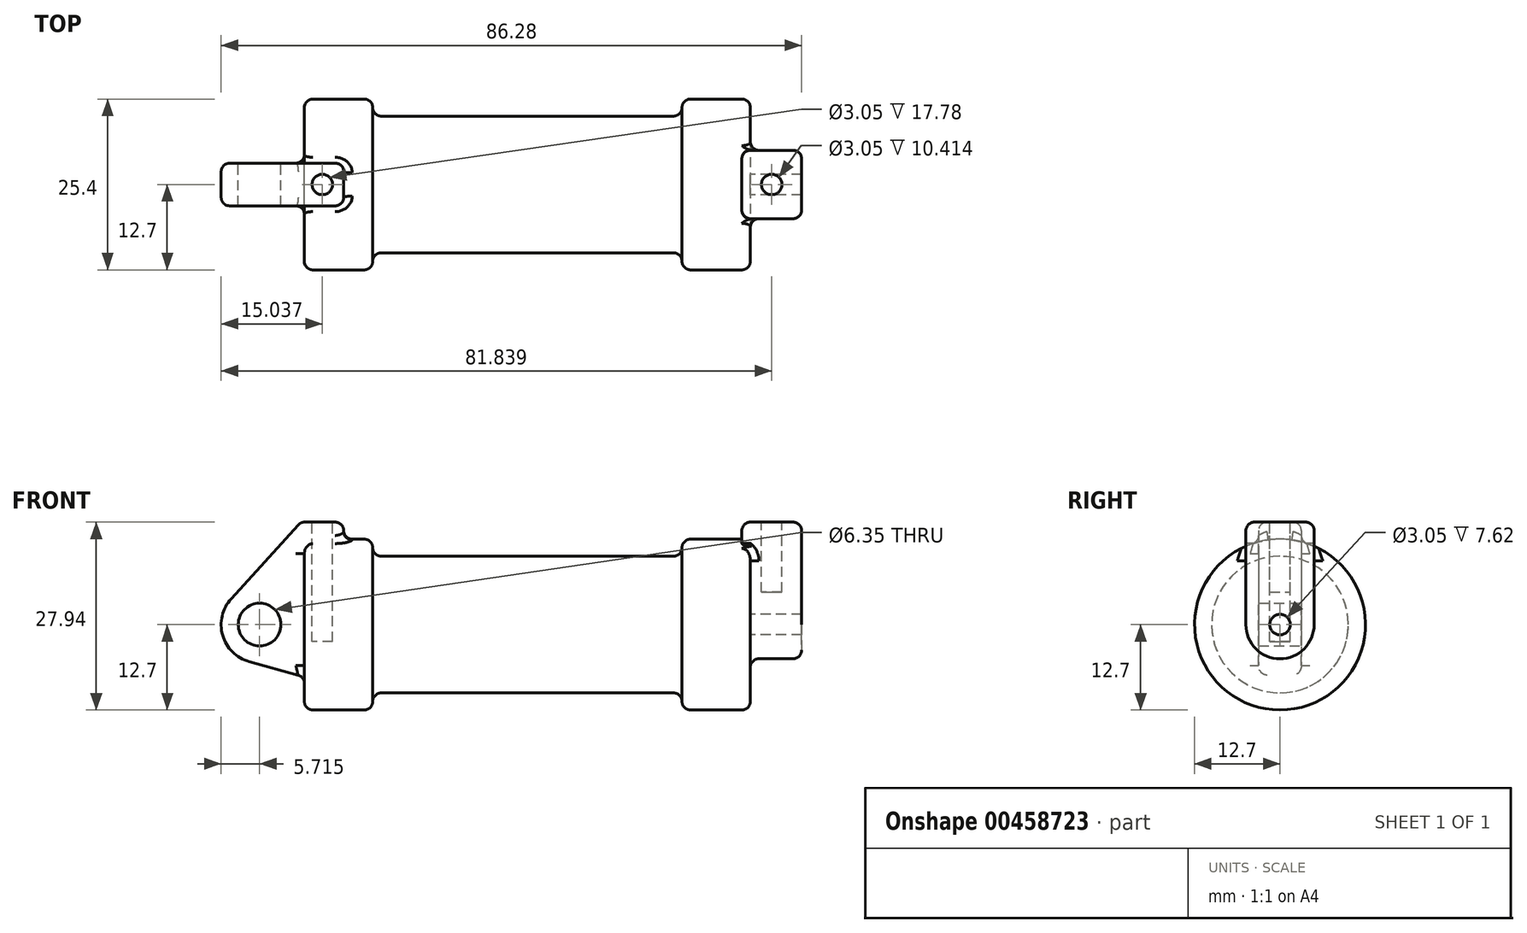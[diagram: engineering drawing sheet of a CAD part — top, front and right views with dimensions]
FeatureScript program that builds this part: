
annotation { "Feature Type Name" : "Feature", "Feature Type Description" : "" }
export const myFeature = defineFeature(function(context is Context, id is Id, definition is map)
    precondition{}
    {
        {
            var Q0;
            Q0=qCreatedBy(makeId("Front.planeOp"),FACE);
            var sketch = newSketch(context, id + "F0", { "sketchPlane" : qUnion([Q0])});
            skLineSegment(sketch, "E0", {"start": v(0, 0) * mm, "end": v(0, 12.7) * mm});
            skLineSegment(sketch, "E1", {"start": v(0, 12.7) * mm, "end": v(10.16, 12.7) * mm});
            skLineSegment(sketch, "E2", {"start": v(10.16, 12.7) * mm, "end": v(10.16, 10.16) * mm});
            skLineSegment(sketch, "E3", {"start": v(10.16, 10.16) * mm, "end": v(56.13, 10.16) * mm});
            skLineSegment(sketch, "E4", {"start": v(56.13, 10.16) * mm, "end": v(56.13, 12.7) * mm});
            skLineSegment(sketch, "E5", {"start": v(56.13, 12.7) * mm, "end": v(66.3, 12.7) * mm});
            skLineSegment(sketch, "E6", {"start": v(66.3, 12.7) * mm, "end": v(66.3, 0) * mm});
            skLineSegment(sketch, "E7", {"start": v(66.3, 0) * mm, "end": v(0, 0) * mm});
            skLineSegment(sketch, "E8", {"start": v(5.84, 15.24) * mm, "end": v(-0.5, 15.24) * mm});
            skLineSegment(sketch, "E9", {"start": v(-0.5, 15.24) * mm, "end": v(-10.88, 3.85) * mm});
            skLineSegment(sketch, "E10", {"start": v(0, 0) * mm, "end": v(-6.65, 0) * mm});
            skCircle(sketch, "E11", {"center": v(-6.65, 0) * mm, "radius": 5.72 * mm});
            skCircle(sketch, "E12", {"center": v(-6.65, 0) * mm, "radius": 3.18 * mm});
            skLineSegment(sketch, "E13", {"start": v(5.84, 15.24) * mm, "end": v(5.84, -9.4) * mm});
            skLineSegment(sketch, "E14", {"start": v(5.84, -9.4) * mm, "end": v(-8.18, -5.5) * mm});
            skSolve(sketch);
        }
        {
            var Q0;
            {var subQ0=sQuery(id+"F0.wireOp",EDGE,"E2");Q0=makeQuery(id+"F0.imprint","IMPRINT",FACE,{"disambiguationData":[TD([[makeQuery(id+"F0.imprint","IMPRINT",EDGE,{"derivedFrom":subQ0}),-1.0]])]});}
            var Q1;
            {var subQ0=sQuery(id+"F0.wireOp",EDGE,"E0");Q1=makeQuery(id+"F0.imprint","IMPRINT",FACE,{"disambiguationData":[TD([[makeQuery(id+"F0.imprint","IMPRINT",EDGE,{"derivedFrom":subQ0}),-1.0]])]});}
            var Q2;
            Q2=sQuery(id+"F0.wireOp",EDGE,"E7");
            revolve(context, id + "F1", {"entities" : qUnion([Q0, Q1]), "axis" : qUnion([Q2]), "revolveType" : RevolveType.FULL});
        }
        {
            var Q0;
            {var subQ1=sQuery(id+"F0.wireOp",EDGE,"E0");Q0=makeQuery(id+"F0.imprint","IMPRINT",FACE,{"disambiguationData":[TD([[makeQuery(id+"F0.imprint","IMPRINT",EDGE,{"derivedFrom":subQ1}),1.0]])]});}
            var Q1;
            {var subQ5=sQuery(id+"F0.wireOp",EDGE,"E12");Q1=makeQuery(id+"F0.imprint","IMPRINT",FACE,{"disambiguationData":[TD([[makeQuery(id+"F0.imprint","IMPRINT",EDGE,{"derivedFrom":subQ5}),-1.0]])]});}
            var Q2;
            {var subQ0=sQuery(id+"F0.wireOp",EDGE,"E14");Q2=makeQuery(id+"F0.imprint","IMPRINT",FACE,{"disambiguationData":[TD([[makeQuery(id+"F0.imprint","IMPRINT",EDGE,{"derivedFrom":subQ0}),-1.0]])]});}
            var Q3;
            {var subQ0=sQuery(id+"F0.wireOp",EDGE,"E0");Q3=makeQuery(id+"F0.imprint","IMPRINT",FACE,{"disambiguationData":[TD([[makeQuery(id+"F0.imprint","IMPRINT",EDGE,{"derivedFrom":subQ0}),-1.0]])]});}
            extrude(context, id + "F2", {"entities" : qUnion([Q0, Q1, Q2, Q3]), "operationType" : NewBodyOperationType.ADD, "depth" : 6.35 * mm, "symmetric" : true});
        }
        {
            var Q0;
            Q0=makeQuery(id+"F1.opRevolve","SWEPT_FACE",FACE,{"disambiguationData":[OSD([sQuery(id+"F0.wireOp",EDGE,"E6")])]});
            var sketch = newSketch(context, id + "F3", { "sketchPlane" : qUnion([Q0])});
            skLineSegment(sketch, "E15", {"start": v(-5.08, 15.23) * mm, "end": v(5.08, 15.23) * mm});
            skLineSegment(sketch, "E16", {"start": v(5.08, 15.23) * mm, "end": v(5.08, -0.01) * mm});
            skLineSegment(sketch, "E17", {"start": v(5.08, -0.01) * mm, "end": v(-5.08, -0.01) * mm});
            skLineSegment(sketch, "E18", {"start": v(-5.08, -0.01) * mm, "end": v(-5.08, 15.23) * mm});
            skCircle(sketch, "E19", {"center": v(0, 0) * mm, "radius": 5.08 * mm});
            skCircle(sketch, "E20", {"center": v(0, 0) * mm, "radius": 1.52 * mm});
            skLineSegment(sketch, "E21.MirrorCS", {"start": v(-5.08, 15.23) * mm, "end": v(-5.08, -0.01) * mm});
            skSolve(sketch);
        }
        {
            var Q0;
            {var subQ0=sQuery(id+"F3.wireOp",EDGE,"E19");var subQ1=sQuery(id+"F3.wireOp",EDGE,"E16");var subQ2=makeQuery(id+"F3.imprint","INTERSECT",VERTEX,{"derivedFrom":[subQ1,subQ0]});Q0=makeQuery(id+"F3.imprint","IMPRINT",FACE,{"disambiguationData":[TD([[makeQuery(id+"F3.imprint","IMPRINT",EDGE,{"disambiguationData":[TD([[subQ2,-1.0]])],"derivedFrom":subQ0}),-1.0]])]});}
            var Q1;
            {var subQ0=sQuery(id+"F3.wireOp",EDGE,"E19");var subQ2=sQuery(id+"F3.wireOp",EDGE,"E17");var subQ3=makeQuery(id+"F3.imprint","INTERSECT",VERTEX,{"derivedFrom":[subQ2,subQ0]});Q1=makeQuery(id+"F3.imprint","IMPRINT",FACE,{"disambiguationData":[TD([[makeQuery(id+"F3.imprint","IMPRINT",EDGE,{"disambiguationData":[TD([[subQ3,-1.0]])],"derivedFrom":subQ2}),-1.0]])]});}
            var Q2;
            {var subQ0=sQuery(id+"F3.wireOp",EDGE,"E19");var subQ1=sQuery(id+"F3.wireOp",EDGE,"E17");var subQ2=makeQuery(id+"F3.imprint","INTERSECT",VERTEX,{"derivedFrom":[subQ1,subQ0]});Q2=makeQuery(id+"F3.imprint","IMPRINT",FACE,{"disambiguationData":[TD([[makeQuery(id+"F3.imprint","IMPRINT",EDGE,{"disambiguationData":[TD([[subQ2,-1.0]])],"derivedFrom":subQ1}),1.0]])]});}
            var Q3;
            {var subQ0=sQuery(id+"F3.wireOp",EDGE,"E15");Q3=makeQuery(id+"F3.imprint","IMPRINT",FACE,{"disambiguationData":[TD([[makeQuery(id+"F3.imprint","IMPRINT",EDGE,{"derivedFrom":subQ0}),-1.0]])]});}
            extrude(context, id + "F4", {"entities" : qUnion([Q0, Q1, Q2, Q3]), "operationType" : NewBodyOperationType.ADD, "depth" : 7.62 * mm});
        }
        {
            var Q0;
            Q0=makeQuery(id+"F4.opExtrude","CAP_FACE",FACE,{"disambiguationData":[OSD([sQuery(id+"F3.wireOp",EDGE,"E15"),sQuery(id+"F3.wireOp",EDGE,"E16"),sQuery(id+"F3.wireOp",EDGE,"E19"),sQuery(id+"F3.wireOp",EDGE,"E20"),sQuery(id+"F3.wireOp",EDGE,"E21.MirrorCS")])],"isStart":true});
            extrude(context, id + "F5", {"entities" : qUnion([Q0]), "operationType" : NewBodyOperationType.ADD, "depth" : 1.27 * mm});
        }
        {
            var Q0;
            Q0=makeQuery(id+"F2.opExtrude","SWEPT_FACE",FACE,{"disambiguationData":[OSD([sQuery(id+"F0.wireOp",EDGE,"E8")])]});
            var sketch = newSketch(context, id + "F6", { "sketchPlane" : qUnion([Q0])});
            skLineSegment(sketch, "E22", {"start": v(2.67, 3.18) * mm, "end": v(2.67, -3.18) * mm, "construction": true});
            skLineSegment(sketch, "E23", {"start": v(-0.5, 0) * mm, "end": v(5.84, 0) * mm, "construction": true});
            skCircle(sketch, "E24", {"center": v(2.67, 0) * mm, "radius": 1.52 * mm});
            skSolve(sketch);
        }
        {
            var Q0;
            Q0=makeQuery(id+"F6.imprint","IMPRINT",FACE,{"disambiguationData":[TD([[makeQuery(id+"F6.imprint","IMPRINT",EDGE,{"derivedFrom":sQuery(id+"F6.wireOp",EDGE,"E24")}),1.0]])]});
            extrude(context, id + "F7", {"entities" : qUnion([Q0]), "operationType" : NewBodyOperationType.REMOVE, "oppositeDirection" : true, "depth" : 17.78 * mm});
        }
        {
            var Q0;
            {var subQ0=sQuery(id+"F3.wireOp",EDGE,"E15");Q0=makeQuery(id+"F5.boolean.opBoolean","MERGE",FACE,{"derivedFrom":[makeQuery(id+"F4.opExtrude","SWEPT_FACE",FACE,{"disambiguationData":[OSD([subQ0])]}),makeQuery(id+"F5.opExtrude","SWEPT_FACE",FACE,{"disambiguationData":[OSD([subQ0])]})]});}
            var sketch = newSketch(context, id + "F8", { "sketchPlane" : qUnion([Q0])});
            skLineSegment(sketch, "E25", {"start": v(65.02, 0) * mm, "end": v(73.91, 0) * mm});
            skCircle(sketch, "E26", {"center": v(69.47, 0) * mm, "radius": 1.52 * mm});
            skSolve(sketch);
        }
        {
            var Q0;
            {var subQ0=sQuery(id+"F8.wireOp",EDGE,"E26");var subQ1=sQuery(id+"F8.wireOp",EDGE,"E25");var subQ2=makeQuery(id+"F8.imprint","INTERSECT",VERTEX,{"disambiguationData":[OD(0.0)],"derivedFrom":[subQ1,subQ0]});Q0=makeQuery(id+"F8.imprint","IMPRINT",FACE,{"disambiguationData":[TD([[makeQuery(id+"F8.imprint","IMPRINT",EDGE,{"disambiguationData":[TD([[subQ2,-1.0]])],"derivedFrom":subQ1}),1.0]])]});}
            var Q1;
            {var subQ0=sQuery(id+"F8.wireOp",EDGE,"E26");var subQ1=sQuery(id+"F8.wireOp",EDGE,"E25");var subQ2=makeQuery(id+"F8.imprint","INTERSECT",VERTEX,{"disambiguationData":[OD(0.0)],"derivedFrom":[subQ1,subQ0]});Q1=makeQuery(id+"F8.imprint","IMPRINT",FACE,{"disambiguationData":[TD([[makeQuery(id+"F8.imprint","IMPRINT",EDGE,{"disambiguationData":[TD([[subQ2,-1.0]])],"derivedFrom":subQ1}),-1.0]])]});}
            extrude(context, id + "F9", {"entities" : qUnion([Q0, Q1]), "operationType" : NewBodyOperationType.REMOVE, "oppositeDirection" : true, "depth" : 10.4 * mm});
        }
        {
            var Q0;
            {var subQ0=sQuery(id+"F0.wireOp",EDGE,"E5");var subQ1=sQuery(id+"F0.wireOp",EDGE,"E6");Q0=makeQuery(id+"F4.boolean.opBoolean","SPLIT",EDGE,{"disambiguationData":[topologyDisambiguationEdgeConnected([makeQuery(id+"F1.opRevolve","SWEPT_FACE",FACE,{"disambiguationData":[OSD([subQ1])]})])],"derivedFrom":makeQuery(id+"F1.opRevolve","SWEPT_EDGE",EDGE,{"disambiguationData":[OSD([subQ0,subQ1])]})});}
            var Q1;
            Q1=makeQuery(id+"F1.opRevolve","SWEPT_EDGE",EDGE,{"disambiguationData":[OSD([sQuery(id+"F0.wireOp",EDGE,"E4"),sQuery(id+"F0.wireOp",EDGE,"E5")])]});
            var Q2;
            Q2=makeQuery(id+"F1.opRevolve","SWEPT_EDGE",EDGE,{"disambiguationData":[OSD([sQuery(id+"F0.wireOp",EDGE,"E1"),sQuery(id+"F0.wireOp",EDGE,"E2")])]});
            var Q3;
            Q3=makeQuery(id+"F1.opRevolve","SWEPT_EDGE",EDGE,{"disambiguationData":[OSD([sQuery(id+"F0.wireOp",EDGE,"E2"),sQuery(id+"F0.wireOp",EDGE,"E3")])]});
            var Q4;
            Q4=makeQuery(id+"F1.opRevolve","SWEPT_EDGE",EDGE,{"disambiguationData":[OSD([sQuery(id+"F0.wireOp",EDGE,"E0"),sQuery(id+"F0.wireOp",EDGE,"E1")])]});
            var Q5;
            Q5=makeQuery(id+"F1.opRevolve","SWEPT_EDGE",EDGE,{"disambiguationData":[OSD([sQuery(id+"F0.wireOp",EDGE,"E3"),sQuery(id+"F0.wireOp",EDGE,"E4")])]});
            fillet(context, id + "F10", {"entities" : qUnion([Q0, Q1, Q2, Q3, Q4, Q5]), "radius" : 1.27 * mm, "tangentPropagation" : true, "allowEdgeOverflow" : false});
        }
        {
            var Q0;
            Q0=makeQuery(id+"F4.opExtrude","CAP_EDGE",EDGE,{"disambiguationData":[OSD([sQuery(id+"F3.wireOp",EDGE,"E15")])],"isStart":false});
            var Q1;
            Q1=makeQuery(id+"F4.opExtrude","SWEPT_EDGE",EDGE,{"disambiguationData":[OSD([sQuery(id+"F3.wireOp",EDGE,"E15"),sQuery(id+"F3.wireOp",EDGE,"E21.MirrorCS")])]});
            var Q2;
            Q2=makeQuery(id+"F4.opExtrude","CAP_EDGE",EDGE,{"disambiguationData":[OSD([sQuery(id+"F3.wireOp",EDGE,"E21.MirrorCS")])],"isStart":false});
            var Q3;
            Q3=makeQuery(id+"F4.opExtrude","CAP_EDGE",EDGE,{"disambiguationData":[OSD([sQuery(id+"F3.wireOp",EDGE,"E16")])],"isStart":false});
            var Q4;
            Q4=makeQuery(id+"F4.opExtrude","CAP_EDGE",EDGE,{"disambiguationData":[OSD([sQuery(id+"F3.wireOp",EDGE,"E19")])],"isStart":false});
            var Q5;
            Q5=makeQuery(id+"F4.opExtrude","CAP_EDGE",EDGE,{"disambiguationData":[OSD([sQuery(id+"F3.wireOp",EDGE,"E19")])],"isStart":true});
            var Q6;
            {var subQ0=sQuery(id+"F3.wireOp",EDGE,"E16");Q6=makeQuery(id+"F4.boolean.opBoolean","SPLIT",EDGE,{"disambiguationData":[topologyDisambiguationEdgeConnected([makeQuery(id+"F1.opRevolve","SWEPT_FACE",FACE,{"disambiguationData":[OSD([sQuery(id+"F0.wireOp",EDGE,"E6")])]})])],"derivedFrom":makeQuery(id+"F4.opExtrude","CAP_EDGE",EDGE,{"disambiguationData":[OSD([subQ0])],"isStart":true})});}
            var Q7;
            Q7=makeQuery(id+"F5.opExtrude","SWEPT_EDGE",EDGE,{"disambiguationData":[OSD([sQuery(id+"F3.wireOp",EDGE,"E15"),sQuery(id+"F3.wireOp",EDGE,"E21.MirrorCS")])]});
            var Q8;
            Q8=makeQuery(id+"F10.opFillet","BLEND_FACE",FACE,{"disambiguationData":[OSD([sQuery(id+"F0.wireOp",EDGE,"E5"),sQuery(id+"F0.wireOp",EDGE,"E6")])]});
            var Q9;
            {var subQ0=sQuery(id+"F3.wireOp",EDGE,"E21.MirrorCS");var subQ1=sQuery(id+"F0.wireOp",EDGE,"E5");var subQ2=sQuery(id+"F0.wireOp",EDGE,"E6");Q9=makeQuery(id+"F10.opFillet","BLEND_EDGE",EDGE,{"blendedFrom":[makeQuery(id+"F4.boolean.opBoolean","SPLIT",EDGE,{"disambiguationData":[topologyDisambiguationEdgeConnected([makeQuery(id+"F1.opRevolve","SWEPT_FACE",FACE,{"disambiguationData":[OSD([subQ2])]})])],"derivedFrom":makeQuery(id+"F1.opRevolve","SWEPT_EDGE",EDGE,{"disambiguationData":[OSD([subQ1,subQ2])]})}),makeQuery(id+"F5.boolean.opBoolean","MERGE",FACE,{"derivedFrom":[makeQuery(id+"F4.opExtrude","SWEPT_FACE",FACE,{"disambiguationData":[OSD([subQ0])]}),makeQuery(id+"F5.opExtrude","SWEPT_FACE",FACE,{"disambiguationData":[OSD([subQ0])]})]})],"blendedInto":[makeQuery(id+"F5.boolean.opBoolean","MERGE",FACE,{"derivedFrom":[makeQuery(id+"F4.opExtrude","SWEPT_FACE",FACE,{"disambiguationData":[OSD([subQ0])]}),makeQuery(id+"F5.opExtrude","SWEPT_FACE",FACE,{"disambiguationData":[OSD([subQ0])]})]})]});}
            var Q10;
            Q10=makeQuery(id+"F5.opExtrude","CAP_EDGE",EDGE,{"disambiguationData":[OSD([sQuery(id+"F3.wireOp",EDGE,"E15")])],"isStart":false});
            var Q11;
            {var subQ0=sQuery(id+"F3.wireOp",EDGE,"E16");var subQ1=sQuery(id+"F3.wireOp",EDGE,"E15");Q11=makeQuery(id+"F5.boolean.opBoolean","MERGE",EDGE,{"derivedFrom":[makeQuery(id+"F4.opExtrude","SWEPT_EDGE",EDGE,{"disambiguationData":[OSD([subQ1,subQ0])]}),makeQuery(id+"F5.opExtrude","SWEPT_EDGE",EDGE,{"disambiguationData":[OSD([subQ1,subQ0])]})]});}
            var Q12;
            {var subQ0=sQuery(id+"F3.wireOp",EDGE,"E21.MirrorCS");Q12=makeQuery(id+"F4.boolean.opBoolean","SPLIT",EDGE,{"disambiguationData":[topologyDisambiguationEdgeConnected([makeQuery(id+"F1.opRevolve","SWEPT_FACE",FACE,{"disambiguationData":[OSD([sQuery(id+"F0.wireOp",EDGE,"E6")])]})])],"derivedFrom":makeQuery(id+"F4.opExtrude","CAP_EDGE",EDGE,{"disambiguationData":[OSD([subQ0])],"isStart":true})});}
            var Q13;
            {var subQ0=sQuery(id+"F3.wireOp",EDGE,"E16");var subQ1=sQuery(id+"F0.wireOp",EDGE,"E5");var subQ2=sQuery(id+"F0.wireOp",EDGE,"E6");Q13=makeQuery(id+"F10.opFillet","BLEND_EDGE",EDGE,{"blendedFrom":[makeQuery(id+"F4.boolean.opBoolean","SPLIT",EDGE,{"disambiguationData":[topologyDisambiguationEdgeConnected([makeQuery(id+"F1.opRevolve","SWEPT_FACE",FACE,{"disambiguationData":[OSD([subQ2])]})])],"derivedFrom":makeQuery(id+"F1.opRevolve","SWEPT_EDGE",EDGE,{"disambiguationData":[OSD([subQ1,subQ2])]})}),makeQuery(id+"F5.boolean.opBoolean","MERGE",FACE,{"derivedFrom":[makeQuery(id+"F4.opExtrude","SWEPT_FACE",FACE,{"disambiguationData":[OSD([subQ0])]}),makeQuery(id+"F5.opExtrude","SWEPT_FACE",FACE,{"disambiguationData":[OSD([subQ0])]})]})],"blendedInto":[makeQuery(id+"F5.boolean.opBoolean","MERGE",FACE,{"derivedFrom":[makeQuery(id+"F4.opExtrude","SWEPT_FACE",FACE,{"disambiguationData":[OSD([subQ0])]}),makeQuery(id+"F5.opExtrude","SWEPT_FACE",FACE,{"disambiguationData":[OSD([subQ0])]})]})]});}
            fillet(context, id + "F11", {"entities" : qUnion([Q0, Q1, Q2, Q3, Q4, Q5, Q6, Q7, Q8, Q9, Q10, Q11, Q12, Q13]), "radius" : 1.27 * mm, "tangentPropagation" : true, "allowEdgeOverflow" : false});
        }
        {
            var Q0;
            Q0=makeQuery(id+"F5.opExtrude","CAP_EDGE",EDGE,{"disambiguationData":[OSD([sQuery(id+"F3.wireOp",EDGE,"E16")])],"isStart":false});
            var Q1;
            Q1=makeQuery(id+"F5.opExtrude","CAP_EDGE",EDGE,{"disambiguationData":[OSD([sQuery(id+"F3.wireOp",EDGE,"E21.MirrorCS")])],"isStart":false});
            var Q2;
            Q2=makeQuery(id+"F2.boolean.opBoolean","INTERSECT",EDGE,{"derivedFrom":[makeQuery(id+"F1.opRevolve","SWEPT_FACE",FACE,{"disambiguationData":[OSD([sQuery(id+"F0.wireOp",EDGE,"E1")])]}),makeQuery(id+"F2.opExtrude","CAP_FACE",FACE,{"disambiguationData":[OSD([sQuery(id+"F0.wireOp",EDGE,"E8"),sQuery(id+"F0.wireOp",EDGE,"E9"),sQuery(id+"F0.wireOp",EDGE,"E11"),sQuery(id+"F0.wireOp",EDGE,"E12"),sQuery(id+"F0.wireOp",EDGE,"E13"),sQuery(id+"F0.wireOp",EDGE,"E14")])],"isStart":true})]});
            var Q3;
            Q3=makeQuery(id+"F2.boolean.opBoolean","INTERSECT",EDGE,{"derivedFrom":[makeQuery(id+"F1.opRevolve","SWEPT_FACE",FACE,{"disambiguationData":[OSD([sQuery(id+"F0.wireOp",EDGE,"E0")])]}),makeQuery(id+"F2.opExtrude","CAP_FACE",FACE,{"disambiguationData":[OSD([sQuery(id+"F0.wireOp",EDGE,"E8"),sQuery(id+"F0.wireOp",EDGE,"E9"),sQuery(id+"F0.wireOp",EDGE,"E11"),sQuery(id+"F0.wireOp",EDGE,"E12"),sQuery(id+"F0.wireOp",EDGE,"E13"),sQuery(id+"F0.wireOp",EDGE,"E14")])],"isStart":true})]});
            var Q4;
            Q4=makeQuery(id+"F10.opFillet","BLEND_EDGE",EDGE,{"blendedFrom":[makeQuery(id+"F1.opRevolve","SWEPT_EDGE",EDGE,{"disambiguationData":[OSD([sQuery(id+"F0.wireOp",EDGE,"E0"),sQuery(id+"F0.wireOp",EDGE,"E1")])]}),makeQuery(id+"F2.opExtrude","CAP_FACE",FACE,{"disambiguationData":[OSD([sQuery(id+"F0.wireOp",EDGE,"E8"),sQuery(id+"F0.wireOp",EDGE,"E9"),sQuery(id+"F0.wireOp",EDGE,"E11"),sQuery(id+"F0.wireOp",EDGE,"E12"),sQuery(id+"F0.wireOp",EDGE,"E13"),sQuery(id+"F0.wireOp",EDGE,"E14")])],"isStart":true})],"blendedInto":[makeQuery(id+"F2.opExtrude","CAP_FACE",FACE,{"disambiguationData":[OSD([sQuery(id+"F0.wireOp",EDGE,"E8"),sQuery(id+"F0.wireOp",EDGE,"E9"),sQuery(id+"F0.wireOp",EDGE,"E11"),sQuery(id+"F0.wireOp",EDGE,"E12"),sQuery(id+"F0.wireOp",EDGE,"E13"),sQuery(id+"F0.wireOp",EDGE,"E14")])],"isStart":true})]});
            var Q5;
            Q5=makeQuery(id+"F2.opExtrude","CAP_EDGE",EDGE,{"disambiguationData":[OSD([sQuery(id+"F0.wireOp",EDGE,"E9")])],"isStart":true});
            var Q6;
            Q6=makeQuery(id+"F2.opExtrude","CAP_EDGE",EDGE,{"disambiguationData":[OSD([sQuery(id+"F0.wireOp",EDGE,"E11")])],"isStart":true});
            var Q7;
            Q7=makeQuery(id+"F2.opExtrude","CAP_EDGE",EDGE,{"disambiguationData":[OSD([sQuery(id+"F0.wireOp",EDGE,"E14")])],"isStart":false});
            var Q8;
            Q8=makeQuery(id+"F2.opExtrude","CAP_EDGE",EDGE,{"disambiguationData":[OSD([sQuery(id+"F0.wireOp",EDGE,"E13")])],"isStart":true});
            var Q9;
            Q9=makeQuery(id+"F2.opExtrude","CAP_EDGE",EDGE,{"disambiguationData":[OSD([sQuery(id+"F0.wireOp",EDGE,"E8")])],"isStart":true});
            var Q10;
            Q10=makeQuery(id+"F2.opExtrude","SWEPT_EDGE",EDGE,{"disambiguationData":[OSD([sQuery(id+"F0.wireOp",EDGE,"E8"),sQuery(id+"F0.wireOp",EDGE,"E9")])]});
            var Q11;
            Q11=makeQuery(id+"F2.opExtrude","SWEPT_EDGE",EDGE,{"disambiguationData":[OSD([sQuery(id+"F0.wireOp",EDGE,"E8"),sQuery(id+"F0.wireOp",EDGE,"E13")])]});
            var Q12;
            Q12=makeQuery(id+"F2.opExtrude","CAP_EDGE",EDGE,{"disambiguationData":[OSD([sQuery(id+"F0.wireOp",EDGE,"E8")])],"isStart":false});
            var Q13;
            Q13=makeQuery(id+"F2.boolean.opBoolean","INTERSECT",EDGE,{"derivedFrom":[makeQuery(id+"F1.opRevolve","SWEPT_FACE",FACE,{"disambiguationData":[OSD([sQuery(id+"F0.wireOp",EDGE,"E1")])]}),makeQuery(id+"F2.opExtrude","CAP_FACE",FACE,{"disambiguationData":[OSD([sQuery(id+"F0.wireOp",EDGE,"E8"),sQuery(id+"F0.wireOp",EDGE,"E9"),sQuery(id+"F0.wireOp",EDGE,"E11"),sQuery(id+"F0.wireOp",EDGE,"E12"),sQuery(id+"F0.wireOp",EDGE,"E13"),sQuery(id+"F0.wireOp",EDGE,"E14")])],"isStart":false})]});
            var Q14;
            Q14=makeQuery(id+"F2.opExtrude","CAP_EDGE",EDGE,{"disambiguationData":[OSD([sQuery(id+"F0.wireOp",EDGE,"E13")])],"isStart":false});
            var Q15;
            Q15=makeQuery(id+"F2.opExtrude","CAP_EDGE",EDGE,{"disambiguationData":[OSD([sQuery(id+"F0.wireOp",EDGE,"E9")])],"isStart":false});
            var Q16;
            Q16=makeQuery(id+"F2.opExtrude","CAP_EDGE",EDGE,{"disambiguationData":[OSD([sQuery(id+"F0.wireOp",EDGE,"E11")])],"isStart":false});
            var Q17;
            Q17=makeQuery(id+"F10.opFillet","BLEND_EDGE",EDGE,{"blendedFrom":[makeQuery(id+"F1.opRevolve","SWEPT_EDGE",EDGE,{"disambiguationData":[OSD([sQuery(id+"F0.wireOp",EDGE,"E0"),sQuery(id+"F0.wireOp",EDGE,"E1")])]}),makeQuery(id+"F2.opExtrude","CAP_FACE",FACE,{"disambiguationData":[OSD([sQuery(id+"F0.wireOp",EDGE,"E8"),sQuery(id+"F0.wireOp",EDGE,"E9"),sQuery(id+"F0.wireOp",EDGE,"E11"),sQuery(id+"F0.wireOp",EDGE,"E12"),sQuery(id+"F0.wireOp",EDGE,"E13"),sQuery(id+"F0.wireOp",EDGE,"E14")])],"isStart":false})],"blendedInto":[makeQuery(id+"F2.opExtrude","CAP_FACE",FACE,{"disambiguationData":[OSD([sQuery(id+"F0.wireOp",EDGE,"E8"),sQuery(id+"F0.wireOp",EDGE,"E9"),sQuery(id+"F0.wireOp",EDGE,"E11"),sQuery(id+"F0.wireOp",EDGE,"E12"),sQuery(id+"F0.wireOp",EDGE,"E13"),sQuery(id+"F0.wireOp",EDGE,"E14")])],"isStart":false})]});
            var Q18;
            Q18=makeQuery(id+"F1.opRevolve","SWEPT_FACE",FACE,{"disambiguationData":[OSD([sQuery(id+"F0.wireOp",EDGE,"E1")])]});
            var Q19;
            Q19=makeQuery(id+"F2.opExtrude","SWEPT_FACE",FACE,{"disambiguationData":[OSD([sQuery(id+"F0.wireOp",EDGE,"E13")])]});
            var Q20;
            Q20=makeQuery(id+"F2.opExtrude","SWEPT_FACE",FACE,{"disambiguationData":[OSD([sQuery(id+"F0.wireOp",EDGE,"E14")])]});
            var Q21;
            {var subQ0=sQuery(id+"F3.wireOp",EDGE,"E15");Q21=makeQuery(id+"F11.opFillet","BLEND_EDGE",EDGE,{"blendedFrom":[makeQuery(id+"F5.opExtrude","CAP_EDGE",EDGE,{"disambiguationData":[OSD([subQ0])],"isStart":false}),makeQuery(id+"F5.opExtrude","CAP_FACE",FACE,{"disambiguationData":[OSD([subQ0,sQuery(id+"F3.wireOp",EDGE,"E16"),sQuery(id+"F3.wireOp",EDGE,"E19"),sQuery(id+"F3.wireOp",EDGE,"E20"),sQuery(id+"F3.wireOp",EDGE,"E21.MirrorCS")])],"isStart":false})],"blendedInto":[makeQuery(id+"F5.opExtrude","CAP_FACE",FACE,{"disambiguationData":[OSD([subQ0,sQuery(id+"F3.wireOp",EDGE,"E16"),sQuery(id+"F3.wireOp",EDGE,"E19"),sQuery(id+"F3.wireOp",EDGE,"E20"),sQuery(id+"F3.wireOp",EDGE,"E21.MirrorCS")])],"isStart":false})]});}
            fillet(context, id + "F12", {"entities" : qUnion([Q0, Q1, Q2, Q3, Q4, Q5, Q6, Q7, Q8, Q9, Q10, Q11, Q12, Q13, Q14, Q15, Q16, Q17, Q18, Q19, Q20, Q21]), "radius" : 1.27 * mm, "tangentPropagation" : true, "allowEdgeOverflow" : false});
        }
    });
